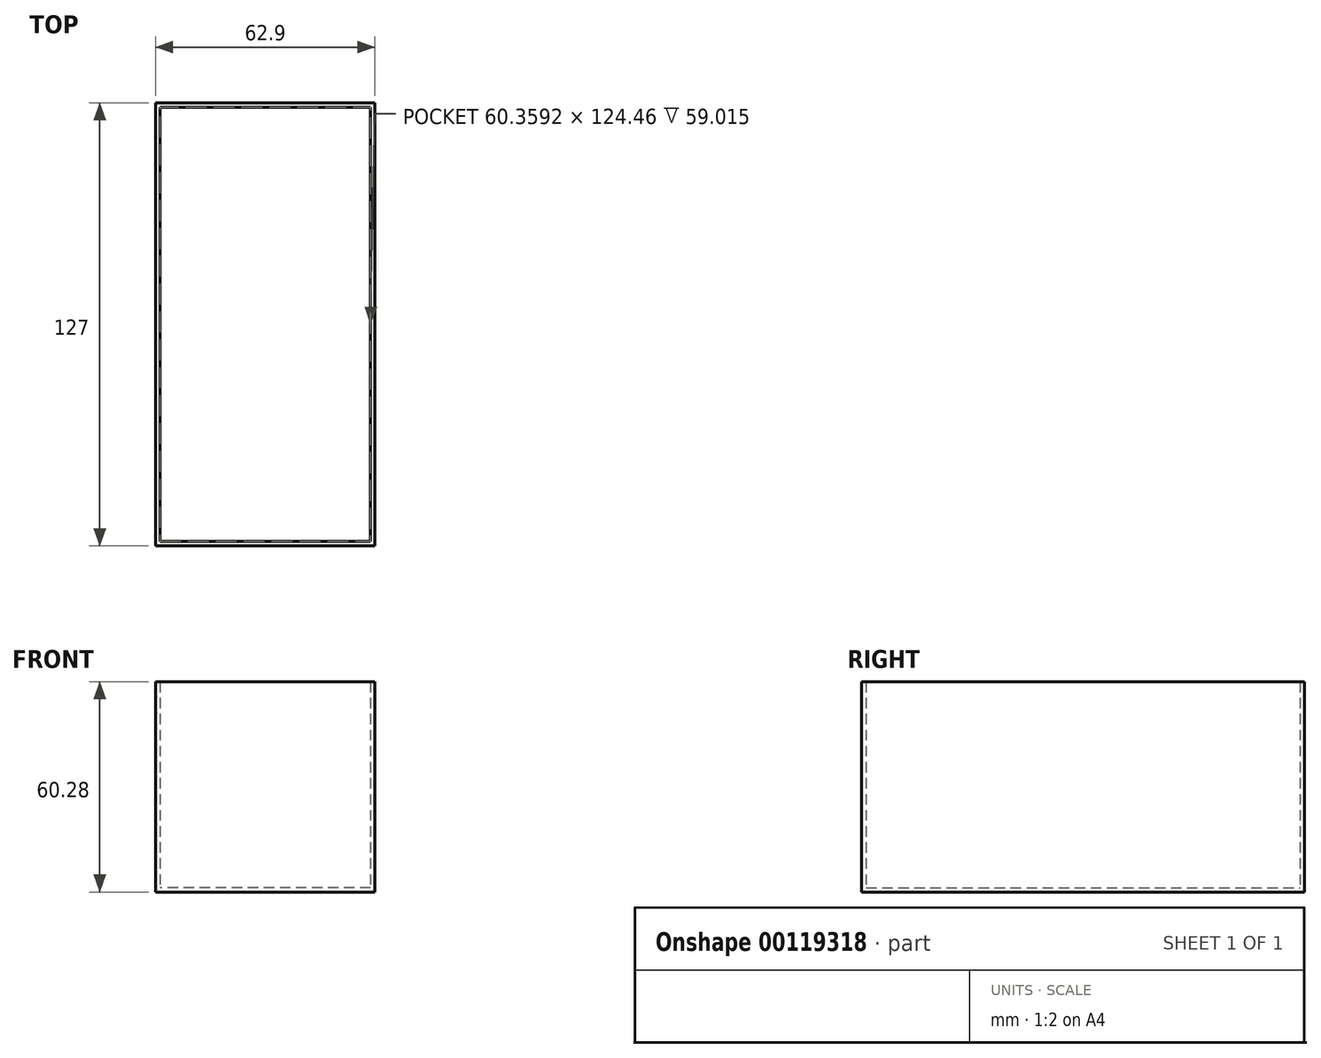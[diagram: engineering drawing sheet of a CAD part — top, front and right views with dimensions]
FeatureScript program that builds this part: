
annotation { "Feature Type Name" : "Feature", "Feature Type Description" : "" }
export const myFeature = defineFeature(function(context is Context, id is Id, definition is map)
    precondition{}
    {
        {
            var Q0;
            Q0=qCreatedBy(makeId("Front.planeOp"),FACE);
            var sketch = newSketch(context, id + "F0", { "sketchPlane" : qUnion([Q0])});
            skLineSegment(sketch, "E0.bottom", {"start": v(31.45, 30.14) * mm, "end": v(-31.45, 30.14) * mm});
            skLineSegment(sketch, "E0.top", {"start": v(31.45, -30.14) * mm, "end": v(-31.45, -30.14) * mm});
            skLineSegment(sketch, "E0.left", {"start": v(31.45, 30.14) * mm, "end": v(31.45, -30.14) * mm});
            skLineSegment(sketch, "E0.right", {"start": v(-31.45, 30.14) * mm, "end": v(-31.45, -30.14) * mm});
            skPoint(sketch, "E0.middle", {"position": v(0, 0) * mm});
            skSolve(sketch);
        }
        {
            var Q0;
            Q0=makeQuery(id+"F0.imprint","IMPRINT",FACE,{"disambiguationData":[TD([[makeQuery(id+"F0.imprint","IMPRINT",EDGE,{"derivedFrom":sQuery(id+"F0.wireOp",EDGE,"E0.bottom")}),1.0]])]});
            extrude(context, id + "F1", {"entities" : qUnion([Q0]), "endBound" : BoundingType.SYMMETRIC, "depth" : 127 * mm});
        }
        {
            var Q0;
            Q0=makeQuery(id+"F1.opExtrude","SWEPT_FACE",FACE,{"disambiguationData":[OSD([sQuery(id+"F0.wireOp",EDGE,"E0.bottom")])]});
            shell(context, id + "F2", {"entities" : qUnion([Q0]), "thickness" : 1.27 * mm});
        }
    });
